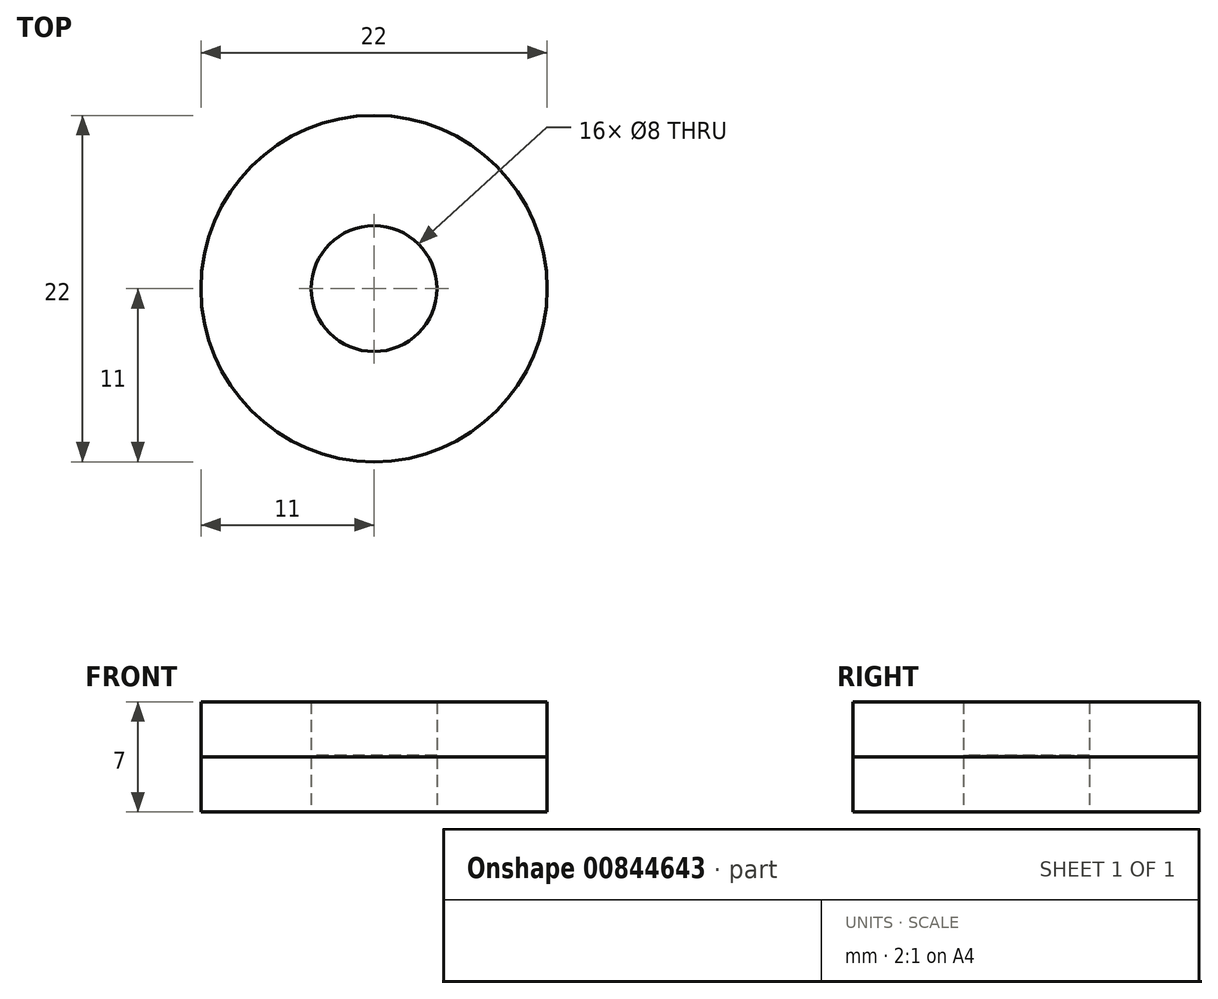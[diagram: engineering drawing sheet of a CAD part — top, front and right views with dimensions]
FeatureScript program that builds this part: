
annotation { "Feature Type Name" : "Feature", "Feature Type Description" : "" }
export const myFeature = defineFeature(function(context is Context, id is Id, definition is map)
    precondition{}
    {
        {
            var Q0;
            Q0=qCreatedBy(makeId("Top.planeOp"),FACE);
            var sketch = newSketch(context, id + "F0", { "sketchPlane" : qUnion([Q0])});
            skCircle(sketch, "E0", {"center": v(0, 0) * mm, "radius": 11 * mm});
            skCircle(sketch, "E1", {"center": v(0, 0) * mm, "radius": 4 * mm});
            skSolve(sketch);
        }
        {
            var Q0;
            Q0=makeQuery(id+"F0.imprint","IMPRINT",FACE,{"disambiguationData":[TD([[makeQuery(id+"F0.imprint","IMPRINT",EDGE,{"derivedFrom":sQuery(id+"F0.wireOp",EDGE,"E0")}),1.0]])]});
            extrude(context, id + "F1", {"entities" : qUnion([Q0]), "depth" : 3.5 * mm, "offsetDistance" : 25.4 * mm});
        }
        {
            var Q0;
            Q0=makeQuery(id+"F1.opExtrude","CAP_FACE",FACE,{"disambiguationData":[OSD([sQuery(id+"F0.wireOp",EDGE,"E0"),sQuery(id+"F0.wireOp",EDGE,"E1")])],"isStart":false});
            var sketch = newSketch(context, id + "F2", { "sketchPlane" : qUnion([Q0])});
            skCircle(sketch, "E2", {"center": v(0, 0) * mm, "radius": 4 * mm});
            skSolve(sketch);
        }
        {
            var Q0;
            Q0=makeQuery(id+"F2.imprint","IMPRINT",FACE,{"disambiguationData":[TD([[makeQuery(id+"F2.imprint","IMPRINT",EDGE,{"derivedFrom":sQuery(id+"F2.wireOp",EDGE,"E2")}),1.0]])]});
            extrude(context, id + "F3", {"entities" : qUnion([Q0]), "depth" : .1 * mm, "offsetDistance" : 25.4 * mm});
        }
        {
            var Q0;
            Q0=makeQuery(id+"F1.opExtrude","CAP_FACE",FACE,{"disambiguationData":[OSD([sQuery(id+"F0.wireOp",EDGE,"E0"),sQuery(id+"F0.wireOp",EDGE,"E1")])],"isStart":false});
            var sketch = newSketch(context, id + "F4", { "sketchPlane" : qUnion([Q0])});
            skCircle(sketch, "E3", {"center": v(0, 0) * mm, "radius": 11 * mm});
            skSolve(sketch);
        }
        {
            var Q0;
            Q0=makeQuery(id+"F4.imprint","IMPRINT",FACE,{"disambiguationData":[TD([[makeQuery(id+"F4.imprint","IMPRINT",EDGE,{"derivedFrom":sQuery(id+"F4.wireOp",EDGE,"E3")}),1.0]])]});
            extrude(context, id + "F5", {"entities" : qUnion([Q0]), "depth" : 3.5 * mm, "offsetDistance" : 25.4 * mm});
        }
    });
